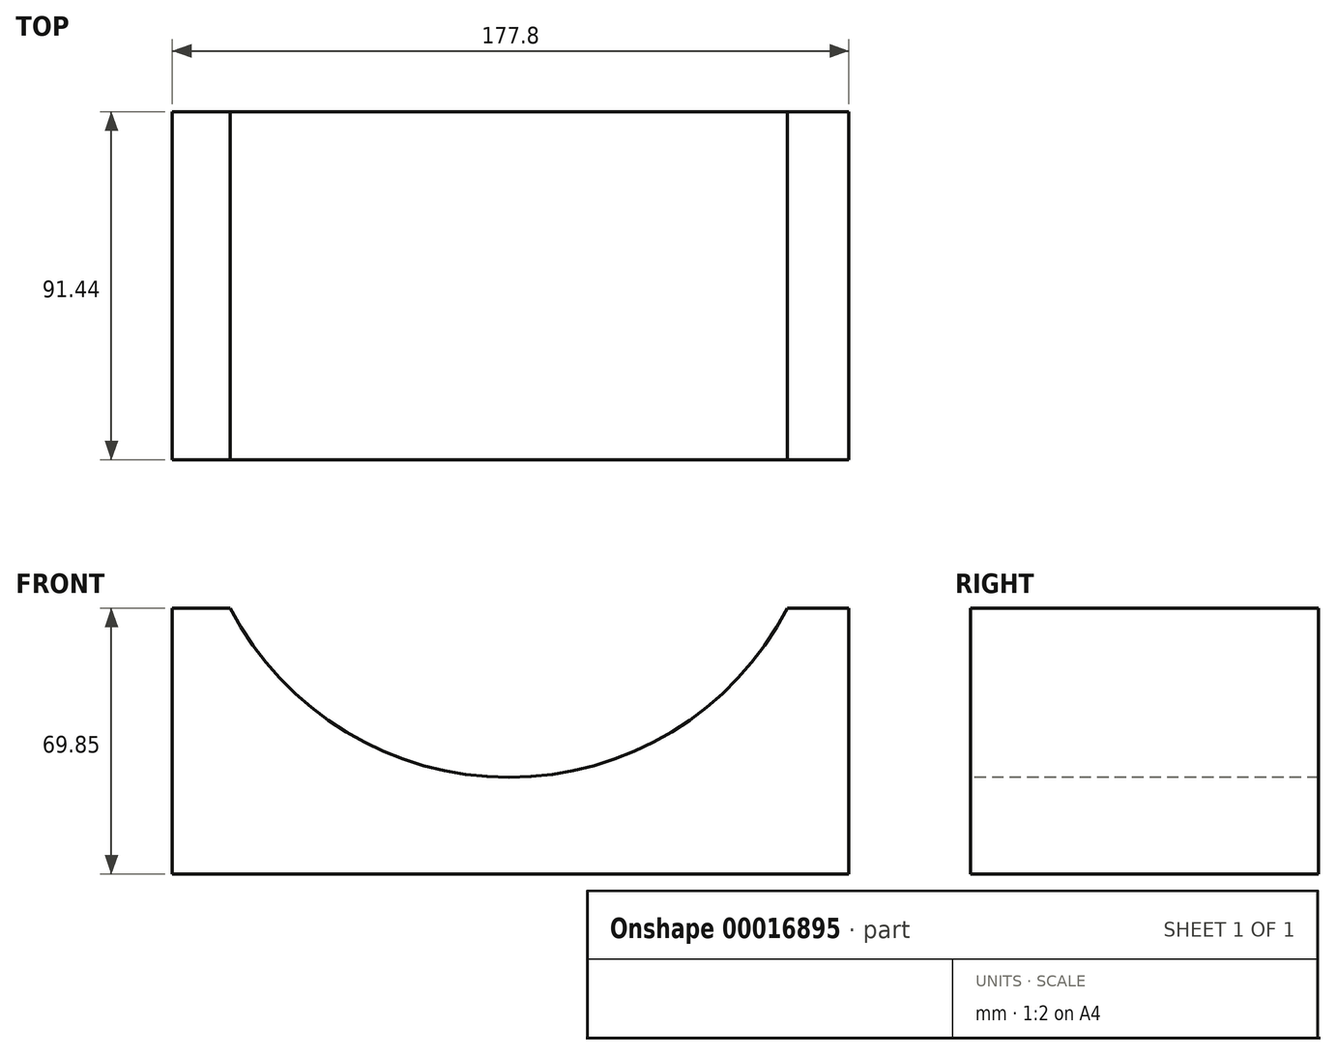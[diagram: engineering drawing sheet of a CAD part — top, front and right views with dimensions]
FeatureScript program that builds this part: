
annotation { "Feature Type Name" : "Feature", "Feature Type Description" : "" }
export const myFeature = defineFeature(function(context is Context, id is Id, definition is map)
    precondition{}
    {
        {
            var Q0;
            Q0=qCreatedBy(makeId("Top.planeOp"),FACE);
            var sketch = newSketch(context, id + "F0", { "sketchPlane" : qUnion([Q0])});
            skLineSegment(sketch, "E0.bottom", {"start": v(-63.02, 43.25) * mm, "end": v(114.78, 43.25) * mm});
            skLineSegment(sketch, "E0.top", {"start": v(-63.02, -48.2) * mm, "end": v(114.78, -48.2) * mm});
            skLineSegment(sketch, "E0.left", {"start": v(-63.02, 43.25) * mm, "end": v(-63.02, -48.2) * mm});
            skLineSegment(sketch, "E0.right", {"start": v(114.78, 43.25) * mm, "end": v(114.78, -48.2) * mm});
            skSolve(sketch);
        }
        {
            var Q0;
            Q0=makeQuery(id+"F0.imprint","IMPRINT",FACE,{"disambiguationData":[TD([[makeQuery(id+"F0.imprint","IMPRINT",EDGE,{"derivedFrom":sQuery(id+"F0.wireOp",EDGE,"E0.bottom")}),-1.0]])]});
            extrude(context, id + "F1", {"entities" : qUnion([Q0]), "depth" : 69.85 * mm});
        }
        {
            var Q0;
            Q0=makeQuery(id+"F1.opExtrude","SWEPT_FACE",FACE,{"disambiguationData":[OSD([sQuery(id+"F0.wireOp",EDGE,"E0.top")])]});
            var sketch = newSketch(context, id + "F2", { "sketchPlane" : qUnion([Q0])});
            skArc(sketch, "E1", {"start": v(-47.78, 69.85) * mm, "mid": v(25.45, 25.4) * mm, "end": v(98.68, 69.85) * mm});
            skLineSegment(sketch, "E2", {"start": v(98.68, 69.85) * mm, "end": v(-47.78, 69.85) * mm});
            skSolve(sketch);
        }
        {
            var Q0;
            Q0=makeQuery(id+"F2.imprint","IMPRINT",FACE,{"disambiguationData":[TD([[makeQuery(id+"F2.imprint","IMPRINT",EDGE,{"derivedFrom":sQuery(id+"F2.wireOp",EDGE,"E1")}),1.0]])]});
            extrude(context, id + "F3", {"entities" : qUnion([Q0]), "operationType" : NewBodyOperationType.REMOVE, "oppositeDirection" : true, "depth" : 91.44 * mm});
        }
    });
